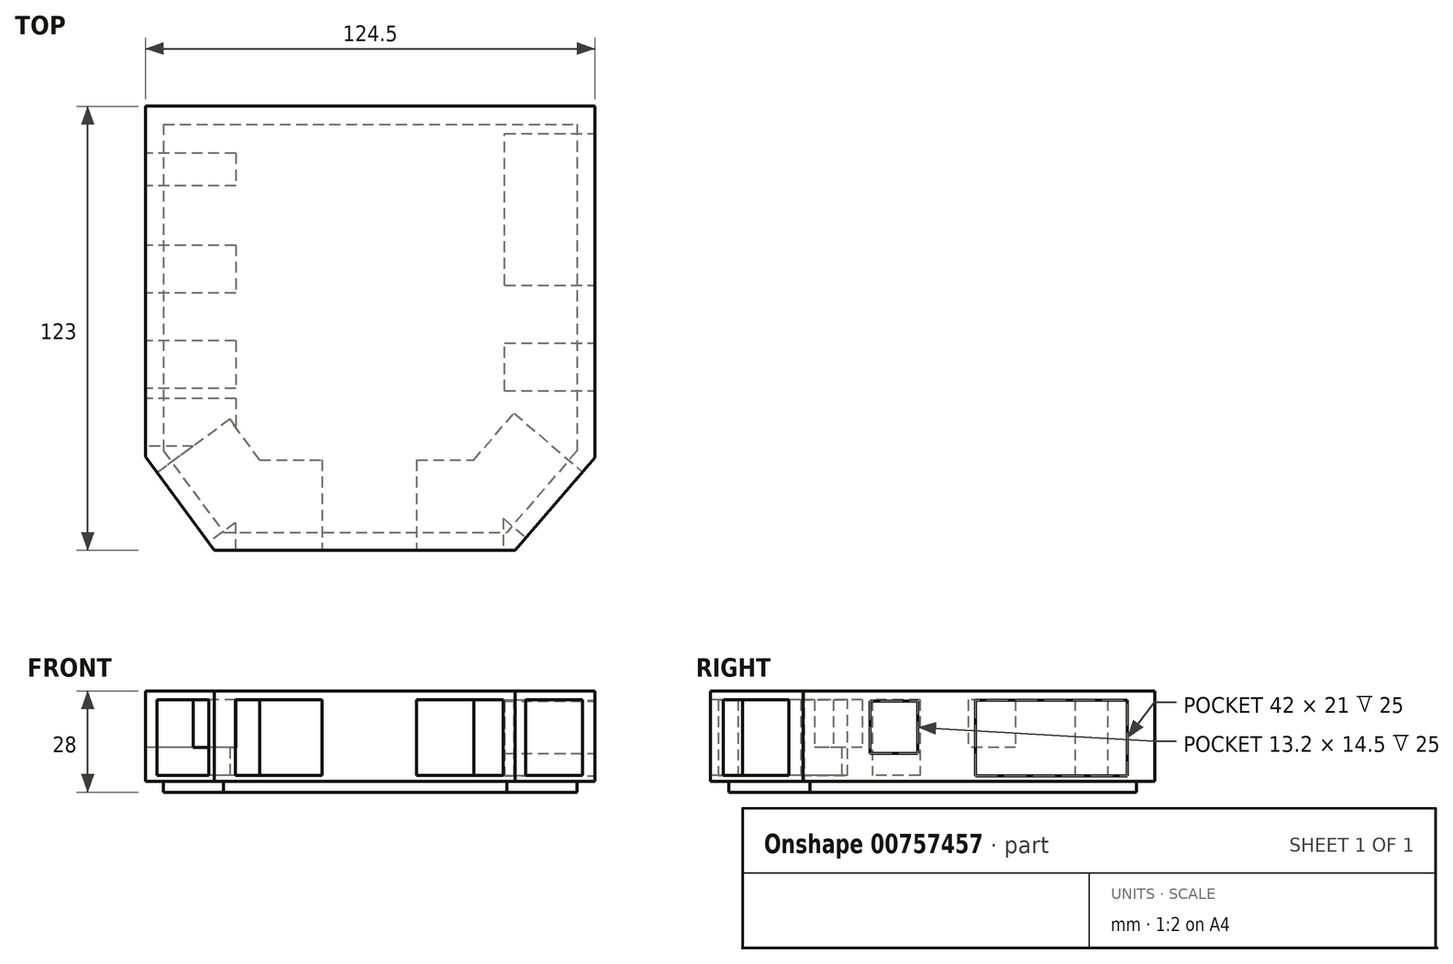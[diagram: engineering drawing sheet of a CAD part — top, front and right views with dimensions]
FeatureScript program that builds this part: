
annotation { "Feature Type Name" : "Feature", "Feature Type Description" : "" }
export const myFeature = defineFeature(function(context is Context, id is Id, definition is map)
    precondition{}
    {
        {
            var Q0;
            Q0=qCreatedBy(makeId("Top.planeOp"),FACE);
            var sketch = newSketch(context, id + "F0", { "sketchPlane" : qUnion([Q0])});
            skLineSegment(sketch, "E0.bottom", {"start": v(-62.07, 49.46) * mm, "end": v(52.43, 49.46) * mm});
            skLineSegment(sketch, "E0.top", {"start": v(-45.47, -63.54) * mm, "end": v(33, -63.54) * mm});
            skLineSegment(sketch, "E0.left", {"start": v(-62.07, 49.46) * mm, "end": v(-62.07, -41.04) * mm});
            skLineSegment(sketch, "E0.right", {"start": v(52.43, 49.46) * mm, "end": v(52.43, -41.04) * mm});
            skLineSegment(sketch, "E1", {"start": v(-62.07, -41.04) * mm, "end": v(-45.47, -63.54) * mm});
            skLineSegment(sketch, "E2", {"start": v(52.43, -41.04) * mm, "end": v(33, -63.54) * mm});
            skPoint(sketch, "E3.orphan", {"position": v(-62.07, -63.54) * mm});
            skPoint(sketch, "E4.orphan", {"position": v(52.43, -63.54) * mm});
            skSolve(sketch);
        }
        {
            var Q0;
            Q0 = qSketchRegion(id + "F0", true);
            extrude(context, id + "F1", {"entities" : qUnion([Q0]), "oppositeDirection" : true, "depth" : 3 * mm, "offsetDistance" : 25 * mm});
        }
        {
            var Q0;
            Q0=makeQuery(id+"F0.imprint","IMPRINT",FACE,{"disambiguationData":[TD([[makeQuery(id+"F0.imprint","IMPRINT",EDGE,{"derivedFrom":sQuery(id+"F0.wireOp",EDGE,"E0.bottom")}),-1.0]])]});
            var sketch = newSketch(context, id + "F2", { "sketchPlane" : qUnion([Q0])});
            skLineSegment(sketch, "E5.0", {"start": v(-62.07, 54.46) * mm, "end": v(52.43, 54.46) * mm});
            skLineSegment(sketch, "E6.0", {"start": v(-67.07, 54.46) * mm, "end": v(-67.07, -42.68) * mm});
            skLineSegment(sketch, "E6.1", {"start": v(-47.99, -68.54) * mm, "end": v(35.29, -68.54) * mm});
            skLineSegment(sketch, "E6.2", {"start": v(35.29, -68.54) * mm, "end": v(57.43, -42.9) * mm});
            skLineSegment(sketch, "E6.3", {"start": v(-67.07, -42.68) * mm, "end": v(-47.99, -68.54) * mm});
            skLineSegment(sketch, "E6.4", {"start": v(57.43, -42.9) * mm, "end": v(57.43, 54.46) * mm});
            skLineSegment(sketch, "E6.5", {"start": v(57.43, 54.46) * mm, "end": v(-67.07, 54.46) * mm});
            skSolve(sketch);
        }
        {
            var Q0;
            Q0 = qSketchRegion(id + "F2", true);
            extrude(context, id + "F3", {"entities" : qUnion([Q0]), "operationType" : NewBodyOperationType.ADD, "depth" : 25 * mm, "offsetDistance" : 25 * mm});
        }
        {
            var Q0;
            Q0=makeQuery(id+"F3.opExtrude","SWEPT_FACE",FACE,{"disambiguationData":[OSD([sQuery(id+"F2.wireOp",EDGE,"E6.4")])]});
            var sketch = newSketch(context, id + "F4", { "sketchPlane" : qUnion([Q0])});
            skLineSegment(sketch, "E7.bottom", {"start": v(4.86, 22.5) * mm, "end": v(46.86, 22.5) * mm});
            skLineSegment(sketch, "E7.top", {"start": v(4.86, 1.5) * mm, "end": v(46.86, 1.5) * mm});
            skLineSegment(sketch, "E7.left", {"start": v(46.86, 22.5) * mm, "end": v(46.86, 1.5) * mm});
            skLineSegment(sketch, "E7.right", {"start": v(4.86, 22.5) * mm, "end": v(4.86, 1.5) * mm});
            skLineSegment(sketch, "E8.bottom", {"start": v(-24.34, 22.2) * mm, "end": v(-11.14, 22.2) * mm});
            skLineSegment(sketch, "E8.top", {"start": v(-24.34, 7.7) * mm, "end": v(-11.14, 7.7) * mm});
            skLineSegment(sketch, "E8.left", {"start": v(-24.34, 22.2) * mm, "end": v(-24.34, 7.7) * mm});
            skLineSegment(sketch, "E8.right", {"start": v(-11.14, 22.2) * mm, "end": v(-11.14, 7.7) * mm});
            skSolve(sketch);
        }
        {
            var Q0;
            Q0=makeQuery(id+"F4.imprint","IMPRINT",FACE,{"disambiguationData":[TD([[makeQuery(id+"F4.imprint","IMPRINT",EDGE,{"derivedFrom":sQuery(id+"F4.wireOp",EDGE,"E8.bottom")}),-1.0]])]});
            var Q1;
            Q1=makeQuery(id+"F4.imprint","IMPRINT",FACE,{"disambiguationData":[TD([[makeQuery(id+"F4.imprint","IMPRINT",EDGE,{"derivedFrom":sQuery(id+"F4.wireOp",EDGE,"E7.bottom")}),-1.0]])]});
            extrude(context, id + "F5", {"entities" : qUnion([Q0, Q1]), "operationType" : NewBodyOperationType.REMOVE, "oppositeDirection" : true, "depth" : 25 * mm, "offsetDistance" : 25 * mm});
        }
        {
            var Q0;
            Q0=makeQuery(id+"F3.opExtrude","SWEPT_FACE",FACE,{"disambiguationData":[OSD([sQuery(id+"F2.wireOp",EDGE,"E6.2")])]});
            var sketch = newSketch(context, id + "F6", { "sketchPlane" : qUnion([Q0])});
            skLineSegment(sketch, "E9.bottom", {"start": v(-24.2, 1.6) * mm, "end": v(-0.2, 1.6) * mm});
            skLineSegment(sketch, "E9.top", {"start": v(-24.2, 22.6) * mm, "end": v(-0.2, 22.6) * mm});
            skLineSegment(sketch, "E9.left", {"start": v(-24.2, 1.6) * mm, "end": v(-24.2, 22.6) * mm});
            skLineSegment(sketch, "E9.right", {"start": v(-0.2, 1.6) * mm, "end": v(-0.2, 22.6) * mm});
            skSolve(sketch);
        }
        {
            var Q0;
            Q0=makeQuery(id+"F6.imprint","IMPRINT",FACE,{"disambiguationData":[TD([[makeQuery(id+"F6.imprint","IMPRINT",EDGE,{"derivedFrom":sQuery(id+"F6.wireOp",EDGE,"E9.bottom")}),1.0]])]});
            extrude(context, id + "F7", {"entities" : qUnion([Q0]), "operationType" : NewBodyOperationType.REMOVE, "oppositeDirection" : true, "depth" : 25 * mm, "offsetDistance" : 25 * mm});
        }
        {
            var Q0;
            Q0=makeQuery(id+"F3.opExtrude","SWEPT_FACE",FACE,{"disambiguationData":[OSD([sQuery(id+"F2.wireOp",EDGE,"E6.1")])]});
            var sketch = newSketch(context, id + "F8", { "sketchPlane" : qUnion([Q0])});
            skLineSegment(sketch, "E10.bottom", {"start": v(8.05, 22.6) * mm, "end": v(32.05, 22.6) * mm});
            skLineSegment(sketch, "E10.top", {"start": v(8.05, 1.6) * mm, "end": v(32.05, 1.6) * mm});
            skLineSegment(sketch, "E10.left", {"start": v(8.05, 22.6) * mm, "end": v(8.05, 1.6) * mm});
            skLineSegment(sketch, "E10.right", {"start": v(32.05, 22.6) * mm, "end": v(32.05, 1.6) * mm});
            skLineSegment(sketch, "E11.bottom", {"start": v(-42.14, 22.6) * mm, "end": v(-18.14, 22.6) * mm});
            skLineSegment(sketch, "E11.top", {"start": v(-42.14, 1.6) * mm, "end": v(-18.14, 1.6) * mm});
            skLineSegment(sketch, "E11.left", {"start": v(-42.14, 22.6) * mm, "end": v(-42.14, 1.6) * mm});
            skLineSegment(sketch, "E11.right", {"start": v(-18.14, 22.6) * mm, "end": v(-18.14, 1.6) * mm});
            skSolve(sketch);
        }
        {
            var Q0;
            Q0=makeQuery(id+"F8.imprint","IMPRINT",FACE,{"disambiguationData":[TD([[makeQuery(id+"F8.imprint","IMPRINT",EDGE,{"derivedFrom":sQuery(id+"F8.wireOp",EDGE,"E11.bottom")}),-1.0]])]});
            var Q1;
            Q1=makeQuery(id+"F8.imprint","IMPRINT",FACE,{"disambiguationData":[TD([[makeQuery(id+"F8.imprint","IMPRINT",EDGE,{"derivedFrom":sQuery(id+"F8.wireOp",EDGE,"E10.bottom")}),-1.0]])]});
            extrude(context, id + "F9", {"entities" : qUnion([Q0, Q1]), "operationType" : NewBodyOperationType.REMOVE, "oppositeDirection" : true, "depth" : 25 * mm, "offsetDistance" : 25 * mm});
        }
        {
            var Q0;
            Q0=makeQuery(id+"F3.opExtrude","SWEPT_FACE",FACE,{"disambiguationData":[OSD([sQuery(id+"F2.wireOp",EDGE,"E6.3")])]});
            var sketch = newSketch(context, id + "F10", { "sketchPlane" : qUnion([Q0])});
            skLineSegment(sketch, "E12.bottom", {"start": v(24, 22.6) * mm, "end": v(0, 22.6) * mm});
            skLineSegment(sketch, "E12.top", {"start": v(24, 1.6) * mm, "end": v(0, 1.6) * mm});
            skLineSegment(sketch, "E12.left", {"start": v(24, 22.6) * mm, "end": v(24, 1.6) * mm});
            skLineSegment(sketch, "E12.right", {"start": v(0, 22.6) * mm, "end": v(0, 1.6) * mm});
            skSolve(sketch);
        }
        {
            var Q0;
            Q0=makeQuery(id+"F10.imprint","IMPRINT",FACE,{"disambiguationData":[TD([[makeQuery(id+"F10.imprint","IMPRINT",EDGE,{"derivedFrom":sQuery(id+"F10.wireOp",EDGE,"E12.bottom")}),1.0]])]});
            extrude(context, id + "F11", {"entities" : qUnion([Q0]), "operationType" : NewBodyOperationType.REMOVE, "oppositeDirection" : true, "depth" : 25 * mm, "offsetDistance" : 25 * mm});
        }
        {
            var Q0;
            Q0=makeQuery(id+"F3.opExtrude","SWEPT_FACE",FACE,{"disambiguationData":[OSD([sQuery(id+"F2.wireOp",EDGE,"E6.0")])]});
            var sketch = newSketch(context, id + "F12", { "sketchPlane" : qUnion([Q0])});
            skLineSegment(sketch, "E13.bottom", {"start": v(26.48, 22.6) * mm, "end": v(39.68, 22.6) * mm});
            skLineSegment(sketch, "E13.top", {"start": v(26.48, 9.4) * mm, "end": v(39.68, 9.4) * mm});
            skLineSegment(sketch, "E13.left", {"start": v(26.48, 22.6) * mm, "end": v(26.48, 9.4) * mm});
            skLineSegment(sketch, "E13.right", {"start": v(39.68, 22.6) * mm, "end": v(39.68, 9.4) * mm});
            skLineSegment(sketch, "E14.bottom", {"start": v(10.54, 22.6) * mm, "end": v(23.74, 22.6) * mm});
            skLineSegment(sketch, "E14.top", {"start": v(10.54, 1.6) * mm, "end": v(23.74, 1.6) * mm});
            skLineSegment(sketch, "E14.left", {"start": v(10.54, 22.6) * mm, "end": v(10.54, 1.6) * mm});
            skLineSegment(sketch, "E14.right", {"start": v(23.74, 22.6) * mm, "end": v(23.74, 1.6) * mm});
            skLineSegment(sketch, "E15.bottom", {"start": v(-15.96, 22.6) * mm, "end": v(-2.76, 22.6) * mm});
            skLineSegment(sketch, "E15.top", {"start": v(-15.96, 9.4) * mm, "end": v(-2.76, 9.4) * mm});
            skLineSegment(sketch, "E15.left", {"start": v(-15.96, 22.6) * mm, "end": v(-15.96, 9.4) * mm});
            skLineSegment(sketch, "E15.right", {"start": v(-2.76, 22.6) * mm, "end": v(-2.76, 9.4) * mm});
            skLineSegment(sketch, "E16.bottom", {"start": v(-41.46, 22.6) * mm, "end": v(-32.46, 22.6) * mm});
            skLineSegment(sketch, "E16.top", {"start": v(-41.46, 1.6) * mm, "end": v(-32.46, 1.6) * mm});
            skLineSegment(sketch, "E16.left", {"start": v(-41.46, 22.6) * mm, "end": v(-41.46, 1.6) * mm});
            skLineSegment(sketch, "E16.right", {"start": v(-32.46, 22.6) * mm, "end": v(-32.46, 1.6) * mm});
            skSolve(sketch);
        }
        {
            var Q0;
            Q0=makeQuery(id+"F12.imprint","IMPRINT",FACE,{"disambiguationData":[TD([[makeQuery(id+"F12.imprint","IMPRINT",EDGE,{"derivedFrom":sQuery(id+"F12.wireOp",EDGE,"E16.bottom")}),-1.0]])]});
            var Q1;
            Q1=makeQuery(id+"F12.imprint","IMPRINT",FACE,{"disambiguationData":[TD([[makeQuery(id+"F12.imprint","IMPRINT",EDGE,{"derivedFrom":sQuery(id+"F12.wireOp",EDGE,"E15.bottom")}),-1.0]])]});
            var Q2;
            Q2=makeQuery(id+"F12.imprint","IMPRINT",FACE,{"disambiguationData":[TD([[makeQuery(id+"F12.imprint","IMPRINT",EDGE,{"derivedFrom":sQuery(id+"F12.wireOp",EDGE,"E14.bottom")}),-1.0]])]});
            var Q3;
            Q3=makeQuery(id+"F12.imprint","IMPRINT",FACE,{"disambiguationData":[TD([[makeQuery(id+"F12.imprint","IMPRINT",EDGE,{"derivedFrom":sQuery(id+"F12.wireOp",EDGE,"E13.bottom")}),-1.0]])]});
            extrude(context, id + "F13", {"entities" : qUnion([Q0, Q1, Q2, Q3]), "operationType" : NewBodyOperationType.REMOVE, "oppositeDirection" : true, "depth" : 25 * mm, "offsetDistance" : 25 * mm});
        }
    });
